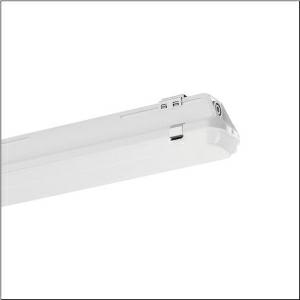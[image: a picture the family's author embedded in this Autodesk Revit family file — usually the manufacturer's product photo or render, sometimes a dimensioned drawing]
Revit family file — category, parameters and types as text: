
# Revit family: monsun_11_51fp20mp4b0u
name_source: partatom
category: Lighting Fixtures
units: mm (PartAtom-declared; Revit-internal decimal feet)

## family parameters
Cut with Voids When Loaded = No
Host = Face
Light Source = No
Part Type = Normal
Room Calculation Point = No
Round Connector Dimension = Use Diameter
Shared = No

## types (1)
- --- (1 x LED, 10910 lm, 62.4 W, 4000K)
    Apparent Load = 62 VA
    CIE Flux Codes = 45 75 93 94 100
    Color Rendering = 80
    Color Temperature = 4000K
    Default Elevation = 1800 mm
    Description = Monsun 11, damp-proof luminaire, chain hanger, primary optical cover: enclosure, of PC, light emission: direct distribution, primary light characteristic: symmetric, installation type: suspended mounting, surface-mounted, horizontal mounting, vertical mounting, LED, rated luminous flux: 10.910lm, luminous efficacy: 175lm/W, light colour: 840, colour temperature: 4000K, control gear: ON/OFF Multilumen, with terminal, 3-pole, max. 2.5mm², mains connection: 220..240V, AC, 50/60Hz, rated input power: 62W, luminaire housing, of glass-fibre reinforced polyester, uncoated, bright grey, incl. chain hanger, length: 1.590mm, width: 90mm, height: 88mm, clip for enclosure, of stainless steel (V2A), ceiling mounting element, of stainless steel (V2A), chain hanger, of stainless steel (V2A), protection rating (complete): IP66, insulation class (complete): insulation class I (protective earthing), certification: CE, ENEC, VDE, UKCA, protection symbol: D, impact resistance: IK08, permissible operating ambient temperature: -35..+35°C, standard: EN 50419, EN 60598-2-1, contact your sales advisor before using the luminaires in applications with unclear chemical exposure, large temperature fluctuations or condensation-forming humidity, LABS conformity tested according to VDMA 24364:2018-05, no direct snow, no direct sun, no direct rain, for indoor or canopied outdoor use, corresponds to IFS (International Featured Standards) requirements for safety and quality in the food industry, packaging unit: 1 piece
    Height = 89 mm
    Lamp = 1 x LED
    Lamp Light Flux = 10910 lm
    Lamp Power = 62.4 W
    Lamp count = 1
    Length = 1590 mm
    Luminous efficacy = 175 lm/W
    Manufacturer = Siteco
    ModVariant = No
    Model = 51FP20MP4B0U
    Mounting Place = Ceiling
    Mounting Type = Surface mounted
    Number of Poles = 1
    OnlyDefault = Yes
    Power Factor = 1
    Product Name = Monsun 11
    Product group = damp-proof luminaire
    ProductGroupID = 300
    Protection Class = Protection class I
    Protection Degree = IP 66
    RLX_Detail_Level = 1
    RLX_Emergency_Light_Flux = 0 lm
    RLX_Emergency_Type = 0
    RLX_Emergency_Type_DB = No
    RlxData = <blob elided: 89973 chars, md5=bb8c3d81>
    Socket = socket
    Standby Power = 0 W
    System Light Flux = 10910 lm
    System Power = 62 W
    Type Comments = factory setting: luminous flux: 100 % | (A | C | E) | 147 mA
    Type Image = l_1349237.jpg
    URL = http://relux.com
    VarID = @adj_000001
    Voltage = 0 V
    Weight = 0.00 kg
    Width = 90 mm

## geometry (parser evidence)
native form markers: Blend x4, Sweep x13
no freeform markers — native parametric forms only
